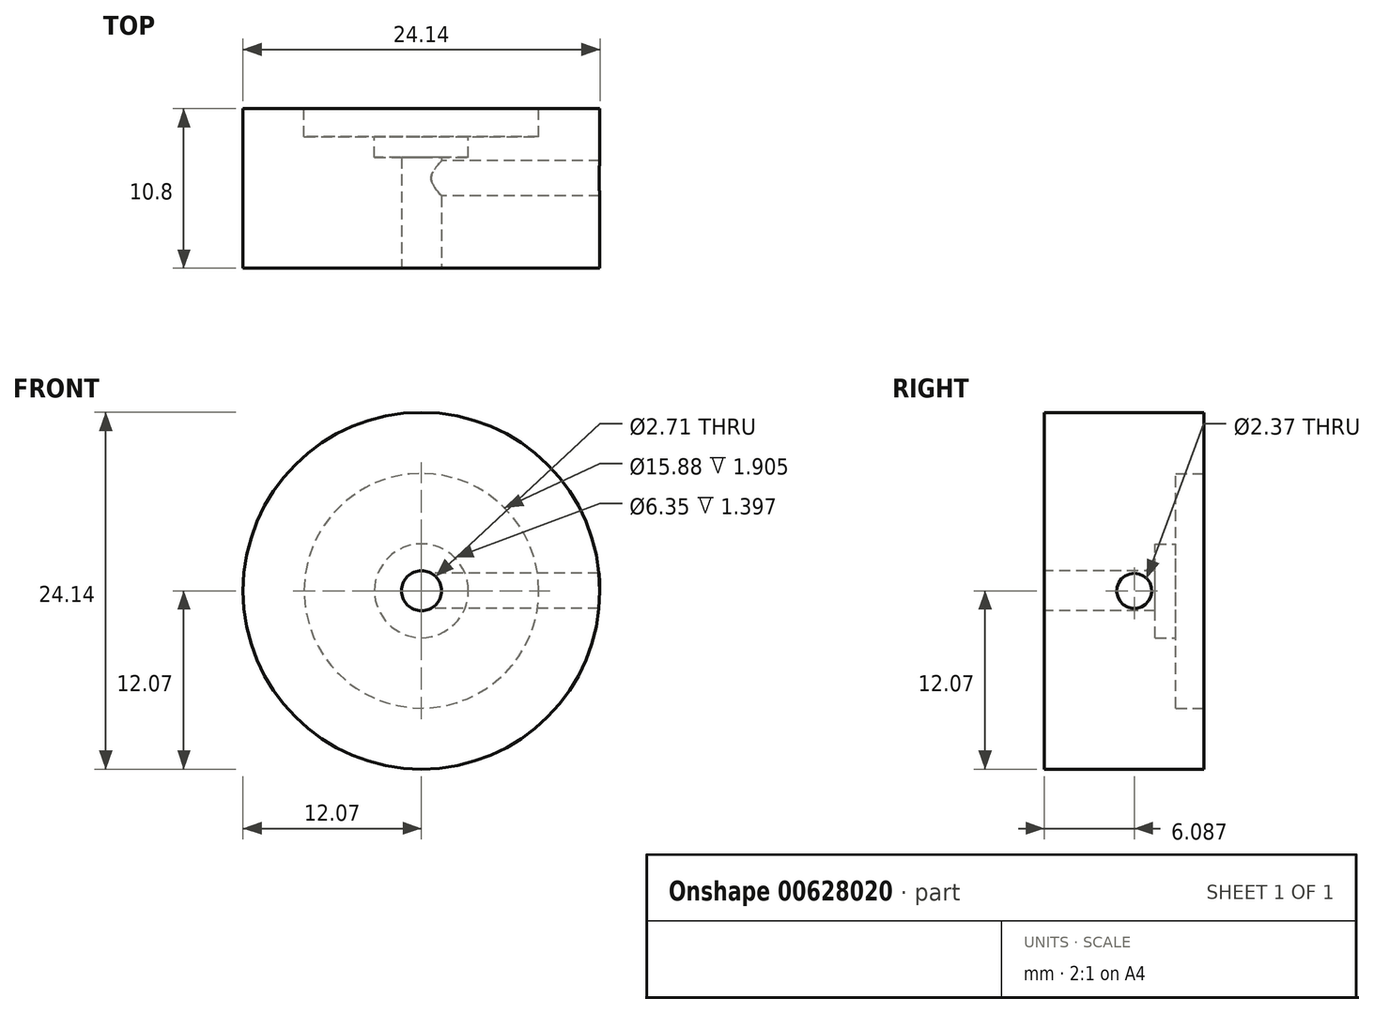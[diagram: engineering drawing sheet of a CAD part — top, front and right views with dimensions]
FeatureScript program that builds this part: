
annotation { "Feature Type Name" : "Feature", "Feature Type Description" : "" }
export const myFeature = defineFeature(function(context is Context, id is Id, definition is map)
    precondition{}
    {
        {
            var Q0;
            Q0=qCreatedBy(makeId("Front.planeOp"),FACE);
            var sketch = newSketch(context, id + "F0", { "sketchPlane" : qUnion([Q0])});
            skCircle(sketch, "E0", {"center": v(0, 0) * mm, "radius": 7.94 * mm, "construction": true});
            skCircle(sketch, "E1", {"center": v(0, 0) * mm, "radius": 12.07 * mm});
            skSolve(sketch);
        }
        {
            var Q0;
            Q0=makeQuery(id+"F0.imprint","IMPRINT",FACE,{"disambiguationData":[TD([[makeQuery(id+"F0.imprint","IMPRINT",EDGE,{"derivedFrom":sQuery(id+"F0.wireOp",EDGE,"E1")}),1.0]])]});
            var Q1;
            Q1=sQuery(id+"F0.wireOp",EDGE,"E0");
            var Q2;
            Q2=sQuery(id+"F0.wireOp",EDGE,"E1");
            extrude(context, id + "F1", {"entities" : qUnion([Q0]), "surfaceEntities" : qUnion([Q1, Q2]), "depth" : 10.8 * mm, "offsetDistance" : 25.4 * mm});
        }
        {
            var Q0;
            Q0=makeQuery(id+"F0.imprint","IMPRINT",FACE,{"disambiguationData":[TD([[makeQuery(id+"F0.imprint","IMPRINT",EDGE,{"derivedFrom":sQuery(id+"F0.wireOp",EDGE,"E1")}),1.0]])]});
            var sketch = newSketch(context, id + "F2", { "sketchPlane" : qUnion([Q0])});
            skCircle(sketch, "E2", {"center": v(0, 0) * mm, "radius": 7.94 * mm});
            skSolve(sketch);
        }
        {
            var Q0;
            Q0=makeQuery(id+"F2.imprint","IMPRINT",FACE,{"disambiguationData":[TD([[makeQuery(id+"F2.imprint","IMPRINT",EDGE,{"derivedFrom":sQuery(id+"F2.wireOp",EDGE,"E2")}),1.0]])]});
            var Q1;
            Q1=sQuery(id+"F2.wireOp",EDGE,"E2");
            extrude(context, id + "F3", {"entities" : qUnion([Q0]), "operationType" : NewBodyOperationType.REMOVE, "surfaceEntities" : qUnion([Q1]), "depth" : 1.9 * mm, "offsetDistance" : 25.4 * mm});
        }
        {
            var Q0;
            Q0=makeQuery(id+"F0.imprint","IMPRINT",FACE,{"disambiguationData":[TD([[makeQuery(id+"F0.imprint","IMPRINT",EDGE,{"derivedFrom":sQuery(id+"F0.wireOp",EDGE,"E1")}),1.0]])]});
            var sketch = newSketch(context, id + "F4", { "sketchPlane" : qUnion([Q0])});
            skCircle(sketch, "E3", {"center": v(0, 0) * mm, "radius": 3.18 * mm});
            skSolve(sketch);
        }
        {
            var Q0;
            Q0 = qSketchRegion(id + "F4", true);
            extrude(context, id + "F5", {"entities" : qUnion([Q0]), "operationType" : NewBodyOperationType.REMOVE, "depth" : 3.3 * mm, "offsetDistance" : 25.4 * mm});
        }
        {
            var Q0;
            Q0=makeQuery(id+"F1.opExtrude","CAP_FACE",FACE,{"disambiguationData":[OSD([sQuery(id+"F0.wireOp",EDGE,"E1")])],"isStart":false});
            var sketch = newSketch(context, id + "F6", { "sketchPlane" : qUnion([Q0])});
            skCircle(sketch, "E4", {"center": v(0, 0) * mm, "radius": 2.38 * mm});
            skSolve(sketch);
        }
        {
            var Q0;
            Q0=sQuery(id+"F6.wireOp",VERTEX,"E4.center");
            var Q1;
            Q1=makeQuery(id+"F1.opExtrude","SWEPT_BODY",BODY,{"disambiguationData":[OSD([sQuery(id+"F0.wireOp",EDGE,"E1")])]});
            hole(context, id + "F7", {"style" : HoleStyle.SIMPLE, "endStyle" : HoleEndStyle.THROUGH, "standardTappedOrClearance" : lookupTablePath({ "standard" : "ANSI", "engagement" : "75%", "pitch" : "32 tpi", "size" : "#6", "type" : "Tapped" }), "standardBlindInLast" : lookupTablePath({ "standard" : "ANSI", "engagement" : "75%", "pitch" : "32 tpi", "size" : "#6", "type" : "Tapped" }), "holeDiameter" : 2.7 * mm, "majorDiameter" : 3.5 * mm, "showTappedDepth" : true, "isTappedThrough" : true, "tappedDepth" : 12.7 * mm, "tapClearance" : 3, "locations" : qUnion([Q0]), "scope" : qUnion([Q1])});
        }
        {
            var Q0;
            Q0=qCreatedBy(makeId("Right.planeOp"),FACE);
            var sketch = newSketch(context, id + "F8", { "sketchPlane" : qUnion([Q0])});
            skCircle(sketch, "E5", {"center": v(-4.71, 0) * mm, "radius": 1.11 * mm});
            skLineSegment(sketch, "E6", {"start": v(-9.53, 12.07) * mm, "end": v(0, 12.07) * mm, "construction": true});
            skSolve(sketch);
        }
        {
            var Q0;
            Q0=sQuery(id+"F8.wireOp",VERTEX,"E5.center");
            var Q1;
            Q1=makeQuery(id+"F1.opExtrude","SWEPT_BODY",BODY,{"disambiguationData":[OSD([sQuery(id+"F0.wireOp",EDGE,"E1")])]});
            hole(context, id + "F9", {"style" : HoleStyle.SIMPLE, "endStyle" : HoleEndStyle.THROUGH, "oppositeDirection" : true, "standardTappedOrClearance" : lookupTablePath({ "standard" : "ANSI", "engagement" : "75%", "pitch" : "48 tpi", "size" : "#4", "type" : "Tapped" }), "standardBlindInLast" : lookupTablePath({ "standard" : "ANSI", "engagement" : "75%", "pitch" : "48 tpi", "size" : "#4", "type" : "Tapped" }), "holeDiameter" : 2.37 * mm, "majorDiameter" : 2.84 * mm, "showTappedDepth" : true, "isTappedThrough" : true, "tappedDepth" : 12.7 * mm, "tapClearance" : 3, "locations" : qUnion([Q0]), "scope" : qUnion([Q1])});
        }
    });
